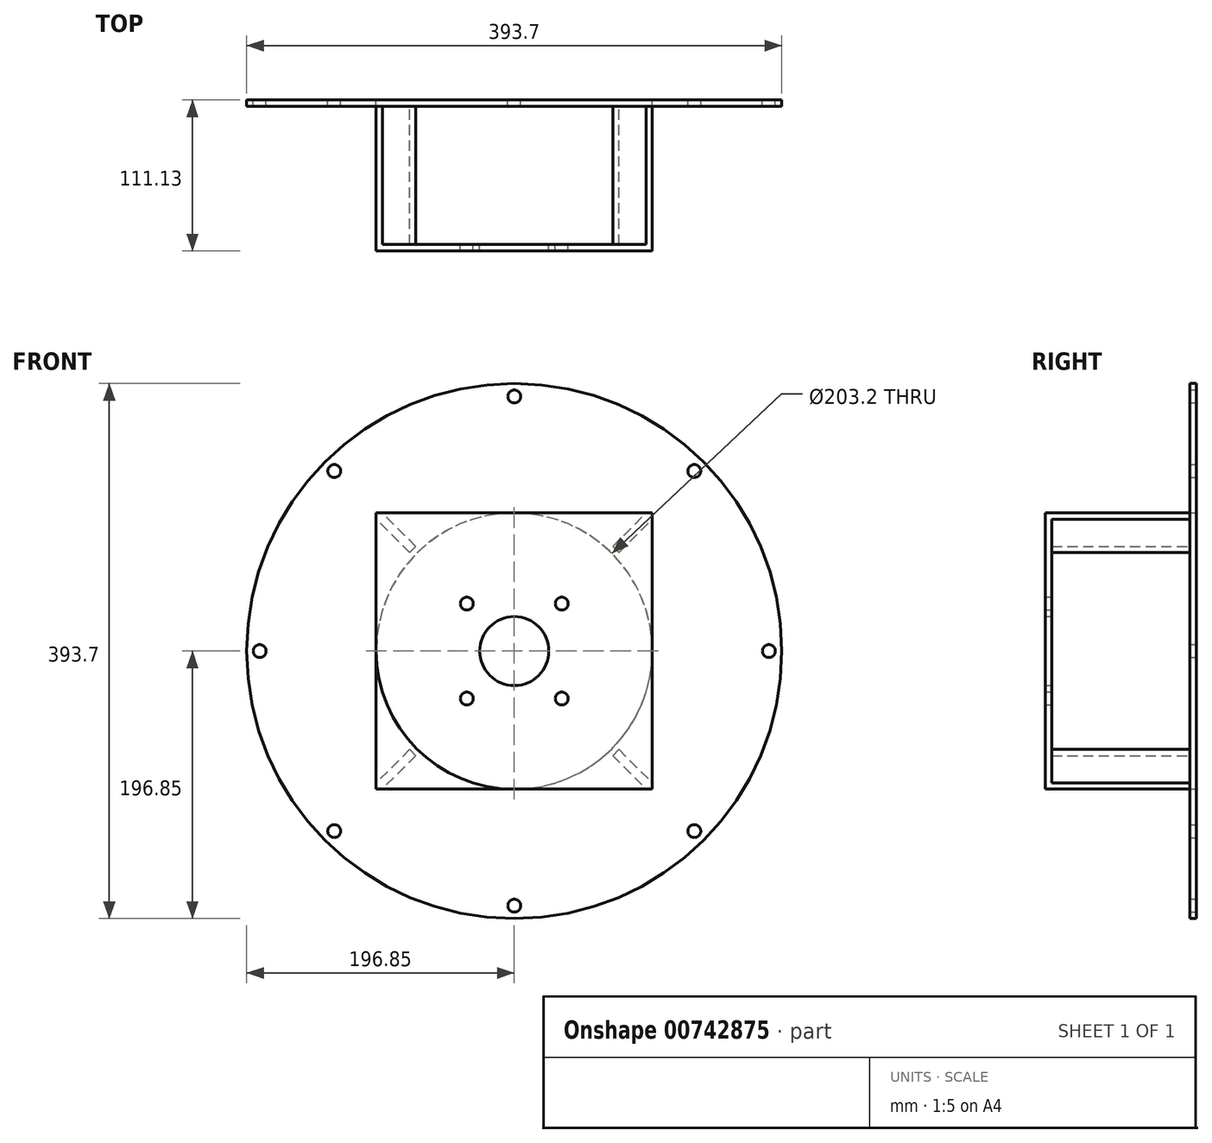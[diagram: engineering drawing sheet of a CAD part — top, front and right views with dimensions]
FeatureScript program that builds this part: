
annotation { "Feature Type Name" : "Feature", "Feature Type Description" : "" }
export const myFeature = defineFeature(function(context is Context, id is Id, definition is map)
    precondition{}
    {
        {
            var Q0;
            Q0=qCreatedBy(makeId("Front.planeOp"),FACE);
            var sketch = newSketch(context, id + "F0", { "sketchPlane" : qUnion([Q0])});
            skCircle(sketch, "E0", {"center": v(0, 0) * mm, "radius": 101.6 * mm});
            skCircle(sketch, "E1", {"center": v(0, 0) * mm, "radius": 177.8 * mm});
            skCircle(sketch, "E2", {"center": v(0, 0) * mm, "radius": 196.85 * mm});
            skLineSegment(sketch, "E3", {"start": v(0, 0) * mm, "end": v(0, 196.85) * mm});
            skLineSegment(sketch, "E4", {"start": v(0, 196.85) * mm, "end": v(0, 187.33) * mm});
            skCircle(sketch, "E5", {"center": v(0, 187.33) * mm, "radius": 4.76 * mm});
            skCircle(sketch, "E6.1.0", {"center": v(-132.46, 132.46) * mm, "radius": 4.76 * mm});
            skCircle(sketch, "E6.2.0", {"center": v(-187.33, 0) * mm, "radius": 4.76 * mm});
            skCircle(sketch, "E6.3.0", {"center": v(-132.46, -132.46) * mm, "radius": 4.76 * mm});
            skCircle(sketch, "E6.4.0", {"center": v(0, -187.33) * mm, "radius": 4.76 * mm});
            skCircle(sketch, "E6.5.0", {"center": v(132.46, -132.46) * mm, "radius": 4.76 * mm});
            skCircle(sketch, "E6.6.0", {"center": v(187.33, 0) * mm, "radius": 4.76 * mm});
            skCircle(sketch, "E6.7.0", {"center": v(132.46, 132.46) * mm, "radius": 4.76 * mm});
            skSolve(sketch);
        }
        {
            var Q0;
            Q0=makeQuery(id+"F0.imprint","IMPRINT",FACE,{"disambiguationData":[TD([[makeQuery(id+"F0.imprint","IMPRINT",EDGE,{"derivedFrom":sQuery(id+"F0.wireOp",EDGE,"E1")}),-1.0]])]});
            var Q1;
            Q1=makeQuery(id+"F0.imprint","IMPRINT",FACE,{"disambiguationData":[TD([[makeQuery(id+"F0.imprint","IMPRINT",EDGE,{"derivedFrom":sQuery(id+"F0.wireOp",EDGE,"E0")}),-1.0]])]});
            extrude(context, id + "F1", {"entities" : qUnion([Q0, Q1]), "depth" : 4.76 * mm, "offsetDistance" : 25.4 * mm});
        }
        {
            var Q0;
            Q0=makeQuery(id+"F1.opExtrude","CAP_FACE",FACE,{"disambiguationData":[OSD([sQuery(id+"F0.wireOp",EDGE,"E0"),sQuery(id+"F0.wireOp",EDGE,"E2"),sQuery(id+"F0.wireOp",EDGE,"E5"),sQuery(id+"F0.wireOp",EDGE,"E6.1.0"),sQuery(id+"F0.wireOp",EDGE,"E6.2.0"),sQuery(id+"F0.wireOp",EDGE,"E6.3.0"),sQuery(id+"F0.wireOp",EDGE,"E6.4.0"),sQuery(id+"F0.wireOp",EDGE,"E6.5.0"),sQuery(id+"F0.wireOp",EDGE,"E6.6.0"),sQuery(id+"F0.wireOp",EDGE,"E6.7.0")])],"isStart":false});
            var sketch = newSketch(context, id + "F2", { "sketchPlane" : qUnion([Q0])});
            skLineSegment(sketch, "E7", {"start": v(0, 0) * mm, "end": v(101.6, 0) * mm});
            skLineSegment(sketch, "E8", {"start": v(101.6, 0) * mm, "end": v(101.6, 101.6) * mm});
            skLineSegment(sketch, "E9", {"start": v(101.6, 101.6) * mm, "end": v(-101.6, 101.6) * mm});
            skLineSegment(sketch, "E10", {"start": v(-101.6, 101.6) * mm, "end": v(-101.6, -101.6) * mm});
            skLineSegment(sketch, "E11", {"start": v(-101.6, -101.6) * mm, "end": v(101.6, -101.6) * mm});
            skLineSegment(sketch, "E12", {"start": v(101.6, -101.6) * mm, "end": v(101.6, 0) * mm});
            skLineSegment(sketch, "E13", {"start": v(-74.66, 74.66) * mm, "end": v(-72.41, 76.9) * mm});
            skLineSegment(sketch, "E14", {"start": v(-72.41, 76.9) * mm, "end": v(-97.1, 101.6) * mm});
            skLineSegment(sketch, "E15", {"start": v(-74.66, 74.66) * mm, "end": v(-76.9, 72.41) * mm});
            skLineSegment(sketch, "E16", {"start": v(-76.9, 72.41) * mm, "end": v(-101.6, 97.1) * mm});
            skLineSegment(sketch, "E17.1.0", {"start": v(-76.9, -72.41) * mm, "end": v(-101.6, -97.1) * mm});
            skLineSegment(sketch, "E17.1.1", {"start": v(-72.41, -76.9) * mm, "end": v(-97.1, -101.6) * mm});
            skLineSegment(sketch, "E17.1.2", {"start": v(-74.66, -74.66) * mm, "end": v(-72.41, -76.9) * mm});
            skLineSegment(sketch, "E17.1.3", {"start": v(-74.66, -74.66) * mm, "end": v(-76.9, -72.41) * mm});
            skLineSegment(sketch, "E17.2.0", {"start": v(72.41, -76.9) * mm, "end": v(97.1, -101.6) * mm});
            skLineSegment(sketch, "E17.2.1", {"start": v(76.9, -72.41) * mm, "end": v(101.6, -97.1) * mm});
            skLineSegment(sketch, "E17.2.2", {"start": v(74.66, -74.66) * mm, "end": v(76.9, -72.41) * mm});
            skLineSegment(sketch, "E17.2.3", {"start": v(74.66, -74.66) * mm, "end": v(72.41, -76.9) * mm});
            skLineSegment(sketch, "E17.3.0", {"start": v(76.9, 72.41) * mm, "end": v(101.6, 97.1) * mm});
            skLineSegment(sketch, "E17.3.1", {"start": v(72.41, 76.9) * mm, "end": v(97.1, 101.6) * mm});
            skLineSegment(sketch, "E17.3.2", {"start": v(74.66, 74.66) * mm, "end": v(72.41, 76.9) * mm});
            skLineSegment(sketch, "E17.3.3", {"start": v(74.66, 74.66) * mm, "end": v(76.9, 72.41) * mm});
            skPoint(sketch, "E17.center", {"position": v(0, 0) * mm});
            skSolve(sketch);
        }
        {
            var Q0;
            Q0=makeQuery(id+"F2.imprint","IMPRINT",FACE,{"disambiguationData":[TD([[makeQuery(id+"F2.imprint","IMPRINT",EDGE,{"derivedFrom":sQuery(id+"F2.wireOp",EDGE,"E13")}),1.0]])]});
            var Q1;
            {var subQ1=sQuery(id+"F2.wireOp",EDGE,"E17.3.0");Q1=makeQuery(id+"F2.imprint","IMPRINT",FACE,{"disambiguationData":[TD([[makeQuery(id+"F2.imprint","IMPRINT",EDGE,{"derivedFrom":subQ1}),1.0]])]});}
            var Q2;
            {var subQ4=sQuery(id+"F2.wireOp",EDGE,"E17.2.0");Q2=makeQuery(id+"F2.imprint","IMPRINT",FACE,{"disambiguationData":[TD([[makeQuery(id+"F2.imprint","IMPRINT",EDGE,{"derivedFrom":subQ4}),1.0]])]});}
            var Q3;
            {var subQ4=sQuery(id+"F2.wireOp",EDGE,"E17.1.0");Q3=makeQuery(id+"F2.imprint","IMPRINT",FACE,{"disambiguationData":[TD([[makeQuery(id+"F2.imprint","IMPRINT",EDGE,{"derivedFrom":subQ4}),1.0]])]});}
            extrude(context, id + "F3", {"entities" : qUnion([Q0, Q1, Q2, Q3]), "operationType" : NewBodyOperationType.ADD, "depth" : 101.6 * mm, "offsetDistance" : 25.4 * mm});
        }
        {
            var Q0;
            Q0=makeQuery(id+"F3.opExtrude","CAP_FACE",FACE,{"disambiguationData":[OSD([sQuery(id+"F2.wireOp",EDGE,"E9"),sQuery(id+"F2.wireOp",EDGE,"E10"),sQuery(id+"F2.wireOp",EDGE,"E13"),sQuery(id+"F2.wireOp",EDGE,"E14"),sQuery(id+"F2.wireOp",EDGE,"E15"),sQuery(id+"F2.wireOp",EDGE,"E16")])],"isStart":false});
            var sketch = newSketch(context, id + "F4", { "sketchPlane" : qUnion([Q0])});
            skLineSegment(sketch, "E18.bottom", {"start": v(-101.6, 101.6) * mm, "end": v(101.6, 101.6) * mm});
            skLineSegment(sketch, "E18.top", {"start": v(-101.6, -101.6) * mm, "end": v(101.6, -101.6) * mm});
            skLineSegment(sketch, "E18.left", {"start": v(-101.6, 101.6) * mm, "end": v(-101.6, -101.6) * mm});
            skLineSegment(sketch, "E18.right", {"start": v(101.6, 101.6) * mm, "end": v(101.6, -101.6) * mm});
            skCircle(sketch, "E19", {"center": v(0, 0) * mm, "radius": 25.4 * mm});
            skLineSegment(sketch, "E20", {"start": v(0, 0) * mm, "end": v(34.93, 0) * mm});
            skLineSegment(sketch, "E21", {"start": v(34.93, 0) * mm, "end": v(34.93, 34.93) * mm});
            skCircle(sketch, "E22", {"center": v(34.93, 34.93) * mm, "radius": 4.76 * mm});
            skCircle(sketch, "E23.1.0", {"center": v(-34.93, 34.93) * mm, "radius": 4.76 * mm});
            skCircle(sketch, "E23.2.0", {"center": v(-34.93, -34.92) * mm, "radius": 4.76 * mm});
            skCircle(sketch, "E23.3.0", {"center": v(34.92, -34.93) * mm, "radius": 4.76 * mm});
            skSolve(sketch);
        }
        {
            var Q0;
            {var subQ2=sQuery(id+"F4.wireOp",EDGE,"E18.top");Q0=makeQuery(id+"F4.imprint","IMPRINT",FACE,{"disambiguationData":[TD([[makeQuery(id+"F4.imprint","IMPRINT",EDGE,{"derivedFrom":subQ2}),1.0]])]});}
            var Q1;
            {var subQ0=makeQuery(id+"F3.opExtrude","CAP_EDGE",EDGE,{"disambiguationData":[OSD([sQuery(id+"F2.wireOp",EDGE,"E14")])],"isStart":false});Q1=makeQuery(id+"F4.imprint","IMPRINT",FACE,{"disambiguationData":[TD([[makeQuery(id+"F4.imprint","IMPRINT",EDGE,{"derivedFrom":subQ0}),1.0]])]});}
            extrude(context, id + "F5", {"entities" : qUnion([Q0, Q1]), "operationType" : NewBodyOperationType.ADD, "depth" : 4.76 * mm, "offsetDistance" : 25.4 * mm});
        }
    });
